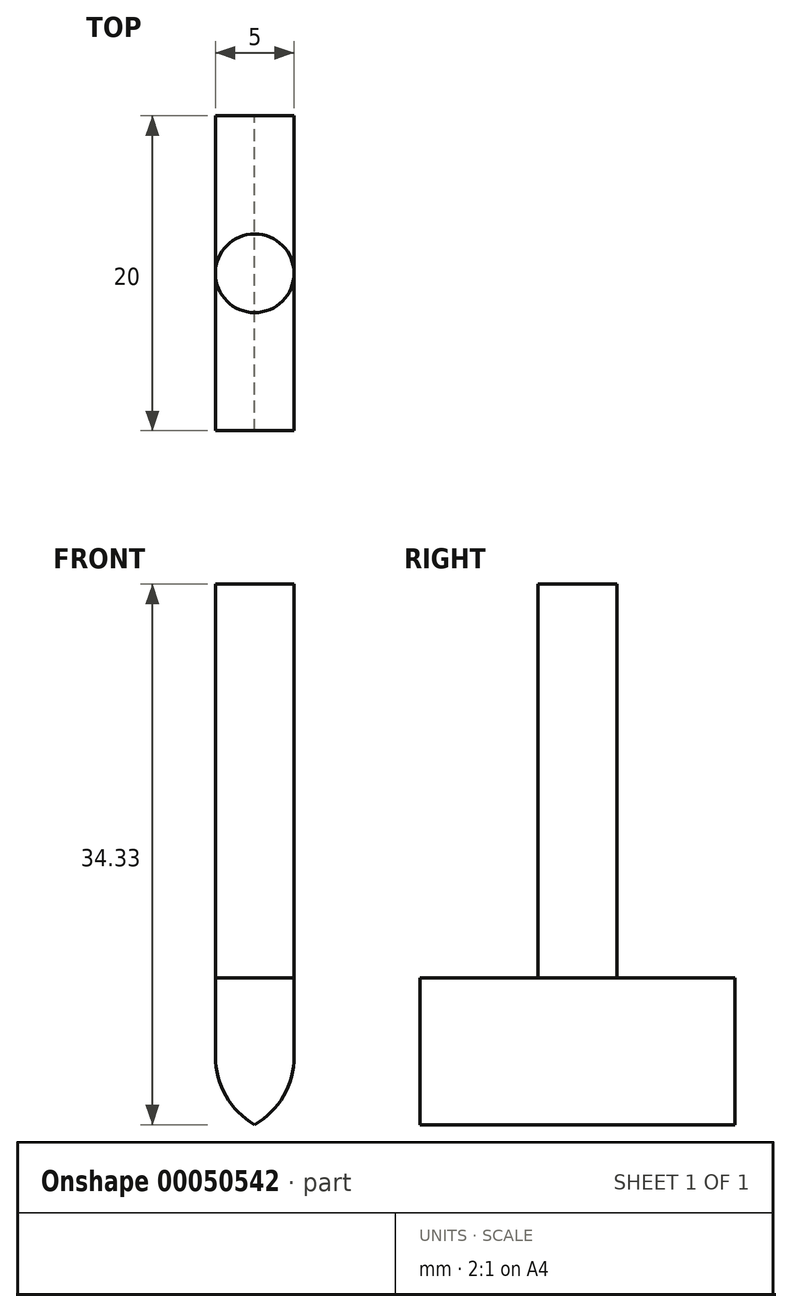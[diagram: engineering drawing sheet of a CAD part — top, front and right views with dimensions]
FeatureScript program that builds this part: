
annotation { "Feature Type Name" : "Feature", "Feature Type Description" : "" }
export const myFeature = defineFeature(function(context is Context, id is Id, definition is map)
    precondition{}
    {
        {
            var Q0;
            Q0=qCreatedBy(makeId("Front.planeOp"),FACE);
            var sketch = newSketch(context, id + "F0", { "sketchPlane" : qUnion([Q0])});
            skLineSegment(sketch, "E0.rect.bottom", {"start": v(-2.5, 5) * mm, "end": v(2.5, 5) * mm});
            skLineSegment(sketch, "E0.rect.top", {"start": v(-2.5, -5) * mm, "end": v(2.5, -5) * mm});
            skLineSegment(sketch, "E0.rect.left", {"start": v(-2.5, 5) * mm, "end": v(-2.5, -5) * mm});
            skLineSegment(sketch, "E0.rect.right", {"start": v(2.5, 5) * mm, "end": v(2.5, -5) * mm});
            skPoint(sketch, "E0.rect.middle", {"position": v(0, 0) * mm});
            skSolve(sketch);
        }
        {
            var Q0;
            Q0=makeQuery(id+"F0.imprint","IMPRINT",FACE,{"disambiguationData":[TD([[makeQuery(id+"F0.imprint","IMPRINT",EDGE,{"derivedFrom":sQuery(id+"F0.wireOp",EDGE,"E0.rect.bottom")}),-1.0]])]});
            extrude(context, id + "F1", {"entities" : qUnion([Q0]), "depth" : 20 * mm});
        }
        {
            var Q0;
            Q0=makeQuery(id+"F1.opExtrude","SWEPT_EDGE",EDGE,{"disambiguationData":[OSD([sQuery(id+"F0.wireOp",EDGE,"E0.rect.top"),sQuery(id+"F0.wireOp",EDGE,"E0.rect.left")])]});
            var Q1;
            Q1=makeQuery(id+"F1.opExtrude","SWEPT_EDGE",EDGE,{"disambiguationData":[OSD([sQuery(id+"F0.wireOp",EDGE,"E0.rect.top"),sQuery(id+"F0.wireOp",EDGE,"E0.rect.right")])]});
            fillet(context, id + "F2", {"entities" : qUnion([Q0, Q1]), "radius" : 5 * mm, "tangentPropagation" : true, "allowEdgeOverflow" : false});
        }
        {
            var Q0;
            Q0=makeQuery(id+"F1.opExtrude","SWEPT_FACE",FACE,{"disambiguationData":[OSD([sQuery(id+"F0.wireOp",EDGE,"E0.rect.bottom")])]});
            var sketch = newSketch(context, id + "F3", { "sketchPlane" : qUnion([Q0])});
            skCircle(sketch, "E1", {"center": v(0, -10) * mm, "radius": 2.5 * mm});
            skSolve(sketch);
        }
        {
            var Q0;
            Q0 = qSketchRegion(id + "F3", true);
            extrude(context, id + "F4", {"entities" : qUnion([Q0]), "operationType" : NewBodyOperationType.ADD, "depth" : 25 * mm});
        }
    });
